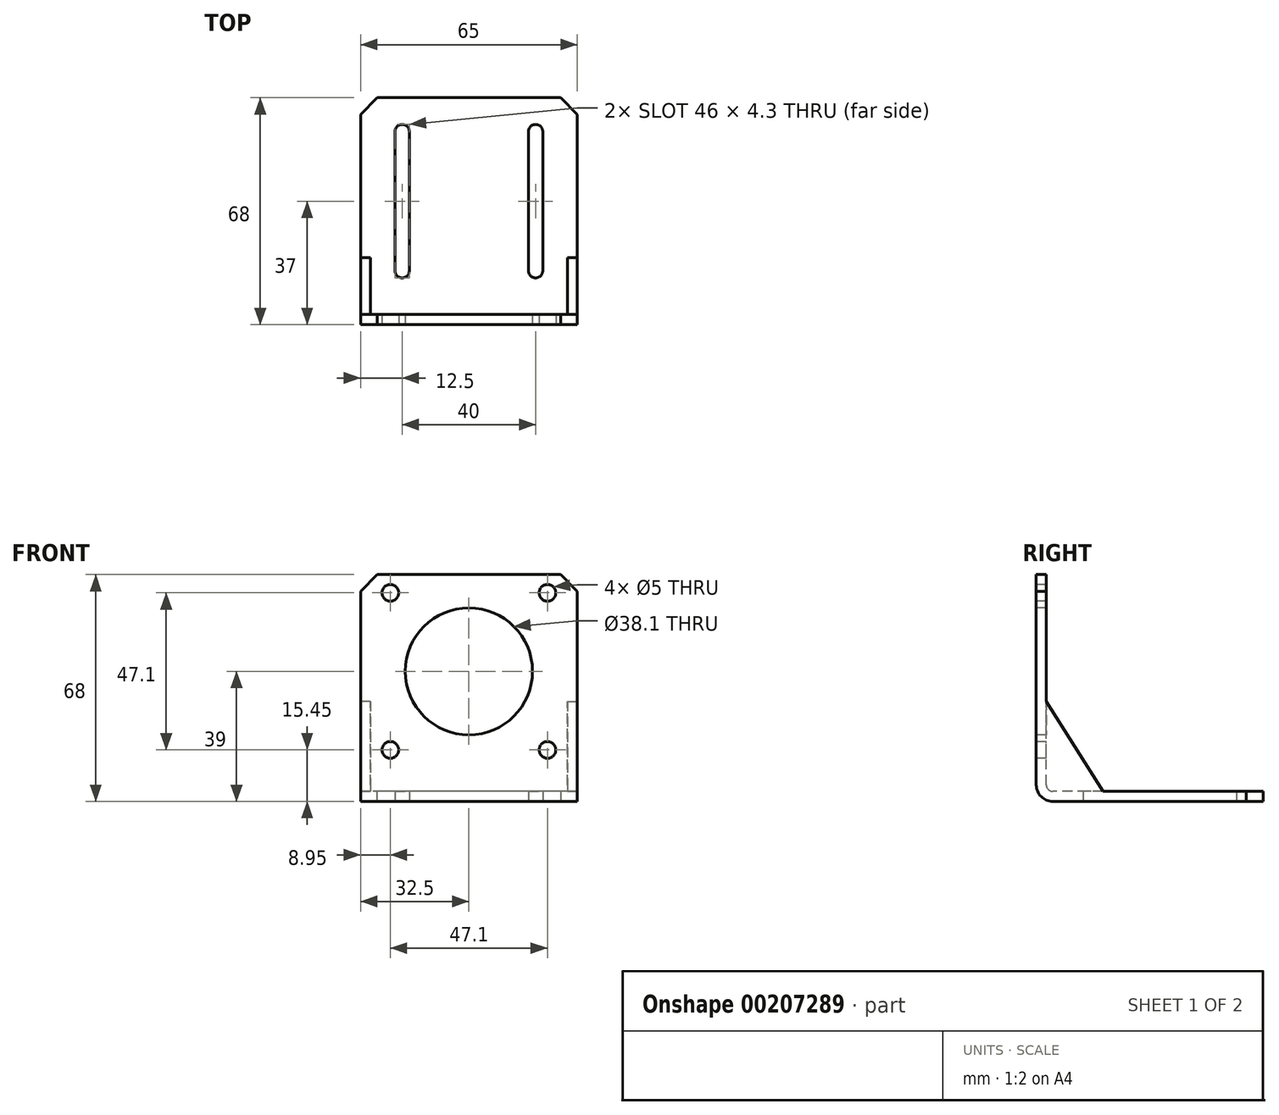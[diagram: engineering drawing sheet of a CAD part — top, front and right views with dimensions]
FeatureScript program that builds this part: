
annotation { "Feature Type Name" : "Feature", "Feature Type Description" : "" }
export const myFeature = defineFeature(function(context is Context, id is Id, definition is map)
    precondition{}
    {
        {
            var Q0;
            Q0=qCreatedBy(makeId("Right.planeOp"),FACE);
            var sketch = newSketch(context, id + "F0", { "sketchPlane" : qUnion([Q0])});
            skLineSegment(sketch, "E0", {"start": v(0, 0) * mm, "end": v(68, 0) * mm});
            skLineSegment(sketch, "E1", {"start": v(68, 0) * mm, "end": v(68, 3) * mm});
            skLineSegment(sketch, "E2", {"start": v(68, 3) * mm, "end": v(3, 3) * mm});
            skLineSegment(sketch, "E3", {"start": v(3, 3) * mm, "end": v(3, 68) * mm});
            skLineSegment(sketch, "E4", {"start": v(3, 68) * mm, "end": v(0, 68) * mm});
            skLineSegment(sketch, "E5", {"start": v(0, 68) * mm, "end": v(0, 0) * mm});
            skSolve(sketch);
        }
        {
            var Q0;
            Q0 = qSketchRegion(id + "F0", true);
            extrude(context, id + "F1", {"entities" : qUnion([Q0]), "endBound" : BoundingType.SYMMETRIC, "depth" : 65 * mm});
        }
        {
            var Q0;
            Q0=makeQuery(id+"F1.opExtrude","SWEPT_EDGE",EDGE,{"disambiguationData":[OSD([sQuery(id+"F0.wireOp",EDGE,"E0"),sQuery(id+"F0.wireOp",EDGE,"E5")])]});
            fillet(context, id + "F2", {"entities" : qUnion([Q0]), "radius" : 5 * mm, "tangentPropagation" : true, "allowEdgeOverflow" : false});
        }
        {
            var Q0;
            Q0=makeQuery(id+"F1.opExtrude","SWEPT_EDGE",EDGE,{"disambiguationData":[OSD([sQuery(id+"F0.wireOp",EDGE,"E2"),sQuery(id+"F0.wireOp",EDGE,"E3")])]});
            fillet(context, id + "F3", {"entities" : qUnion([Q0]), "radius" : 2 * mm, "tangentPropagation" : true, "allowEdgeOverflow" : false});
        }
        {
            var Q0;
            Q0=makeQuery(id+"F1.opExtrude","SWEPT_FACE",FACE,{"disambiguationData":[OSD([sQuery(id+"F0.wireOp",EDGE,"E5")])]});
            var sketch = newSketch(context, id + "F4", { "sketchPlane" : qUnion([Q0])});
            skLineSegment(sketch, "E6", {"start": v(0, 68) * mm, "end": v(0, 39) * mm, "construction": true});
            skPoint(sketch, "E6.endSnap0", {"position": v(0, 68) * mm});
            skLineSegment(sketch, "E7.bottom", {"start": v(23.55, 15.45) * mm, "end": v(-23.55, 15.45) * mm, "construction": true});
            skLineSegment(sketch, "E7.top", {"start": v(23.55, 62.55) * mm, "end": v(-23.55, 62.55) * mm, "construction": true});
            skLineSegment(sketch, "E7.left", {"start": v(23.55, 15.45) * mm, "end": v(23.55, 62.55) * mm, "construction": true});
            skLineSegment(sketch, "E7.right", {"start": v(-23.55, 15.45) * mm, "end": v(-23.55, 62.55) * mm, "construction": true});
            skPoint(sketch, "E7.middle", {"position": v(0, 39) * mm});
            skCircle(sketch, "E8", {"center": v(0, 39) * mm, "radius": 19.05 * mm});
            skCircle(sketch, "E9", {"center": v(-23.55, 15.45) * mm, "radius": 2.5 * mm});
            skCircle(sketch, "E10", {"center": v(23.55, 15.45) * mm, "radius": 2.5 * mm});
            skCircle(sketch, "E11", {"center": v(23.55, 62.55) * mm, "radius": 2.5 * mm});
            skCircle(sketch, "E12", {"center": v(-23.55, 62.55) * mm, "radius": 2.5 * mm});
            skSolve(sketch);
        }
        {
            var Q0;
            Q0 = qSketchRegion(id + "F4", true);
            extrude(context, id + "F5", {"entities" : qUnion([Q0]), "operationType" : NewBodyOperationType.REMOVE, "endBound" : BoundingType.THROUGH_ALL, "oppositeDirection" : true, "depth" : 25 * mm});
        }
        {
            var Q0;
            Q0=makeQuery(id+"F1.opExtrude","SWEPT_FACE",FACE,{"disambiguationData":[OSD([sQuery(id+"F0.wireOp",EDGE,"E0")])]});
            var sketch = newSketch(context, id + "F6", { "sketchPlane" : qUnion([Q0])});
            skLineSegment(sketch, "E13", {"start": v(0, -68) * mm, "end": v(0, -60) * mm, "construction": true});
            skPoint(sketch, "E13.endSnap0", {"position": v(0, -68) * mm});
            skLineSegment(sketch, "E14", {"start": v(-20, -60) * mm, "end": v(20, -60) * mm, "construction": true});
            skLineSegment(sketch, "E15", {"start": v(-20, -60) * mm, "end": v(-20, -57.85) * mm, "construction": true});
            skLineSegment(sketch, "E16", {"start": v(-20, -57.85) * mm, "end": v(-20, -16.15) * mm, "construction": true});
            skLineSegment(sketch, "E17", {"start": v(20, -60) * mm, "end": v(20, -57.85) * mm, "construction": true});
            skLineSegment(sketch, "E18", {"start": v(20, -57.85) * mm, "end": v(20, -16.15) * mm, "construction": true});
            skLineSegment(sketch, "E19", {"start": v(-20, -16.15) * mm, "end": v(-20, -14) * mm, "construction": true});
            skLineSegment(sketch, "E20", {"start": v(20, -16.15) * mm, "end": v(20, -14) * mm, "construction": true});
            skArc(sketch, "E21.0.startCap", {"start": v(-17.85, -57.85) * mm, "mid": v(-20, -60) * mm, "end": v(-22.15, -57.85) * mm});
            skArc(sketch, "E21.0.endCap", {"start": v(-22.15, -16.15) * mm, "mid": v(-20, -14) * mm, "end": v(-17.85, -16.15) * mm});
            skLineSegment(sketch, "E21.0.left", {"start": v(-22.15, -57.85) * mm, "end": v(-22.15, -16.15) * mm});
            skLineSegment(sketch, "E21.0.right", {"start": v(-17.85, -57.85) * mm, "end": v(-17.85, -16.15) * mm});
            skArc(sketch, "E22.0.startCap", {"start": v(22.15, -57.85) * mm, "mid": v(20, -60) * mm, "end": v(17.85, -57.85) * mm});
            skArc(sketch, "E22.0.endCap", {"start": v(17.85, -16.15) * mm, "mid": v(20, -14) * mm, "end": v(22.15, -16.15) * mm});
            skLineSegment(sketch, "E22.0.left", {"start": v(17.85, -57.85) * mm, "end": v(17.85, -16.15) * mm});
            skLineSegment(sketch, "E22.0.right", {"start": v(22.15, -57.85) * mm, "end": v(22.15, -16.15) * mm});
            skSolve(sketch);
        }
        {
            var Q0;
            Q0 = qSketchRegion(id + "F6", true);
            extrude(context, id + "F7", {"entities" : qUnion([Q0]), "operationType" : NewBodyOperationType.REMOVE, "endBound" : BoundingType.THROUGH_ALL, "oppositeDirection" : true, "depth" : 25 * mm});
        }
        {
            var Q0;
            Q0=makeQuery(id+"F1.opExtrude","CAP_FACE",FACE,{"disambiguationData":[OSD([sQuery(id+"F0.wireOp",EDGE,"E0"),sQuery(id+"F0.wireOp",EDGE,"E1"),sQuery(id+"F0.wireOp",EDGE,"E2"),sQuery(id+"F0.wireOp",EDGE,"E3"),sQuery(id+"F0.wireOp",EDGE,"E4"),sQuery(id+"F0.wireOp",EDGE,"E5")])],"isStart":false});
            var sketch = newSketch(context, id + "F8", { "sketchPlane" : qUnion([Q0])});
            skLineSegment(sketch, "E23.0", {"start": v(3, 5) * mm, "end": v(3, 30) * mm});
            skArc(sketch, "E24.0", {"start": v(5, 3) * mm, "mid": v(3.59, 3.59) * mm, "end": v(3, 5) * mm});
            skLineSegment(sketch, "E25.0", {"start": v(20, 3) * mm, "end": v(5, 3) * mm});
            skLineSegment(sketch, "E26", {"start": v(3, 30) * mm, "end": v(20, 3) * mm});
            skPoint(sketch, "E27.orphan", {"position": v(3, 68) * mm});
            skPoint(sketch, "E28.orphan", {"position": v(68, 3) * mm});
            skSolve(sketch);
        }
        {
            var Q0;
            Q0 = qSketchRegion(id + "F8", true);
            extrude(context, id + "F9", {"entities" : qUnion([Q0]), "operationType" : NewBodyOperationType.ADD, "oppositeDirection" : true, "depth" : 3 * mm});
        }
        {
            var Q0;
            Q0=makeQuery(id+"F1.opExtrude","CAP_FACE",FACE,{"disambiguationData":[OSD([sQuery(id+"F0.wireOp",EDGE,"E0"),sQuery(id+"F0.wireOp",EDGE,"E1"),sQuery(id+"F0.wireOp",EDGE,"E2"),sQuery(id+"F0.wireOp",EDGE,"E3"),sQuery(id+"F0.wireOp",EDGE,"E4"),sQuery(id+"F0.wireOp",EDGE,"E5")])],"isStart":true});
            var sketch = newSketch(context, id + "F10", { "sketchPlane" : qUnion([Q0])});
            skLineSegment(sketch, "E29.0.0", {"start": v(-3, 30) * mm, "end": v(-20, 3) * mm});
            skLineSegment(sketch, "E29.0.1", {"start": v(-20, 3) * mm, "end": v(-5, 3) * mm});
            skArc(sketch, "E29.0.2", {"start": v(-5, 3) * mm, "mid": v(-3.59, 3.59) * mm, "end": v(-3, 5) * mm});
            skLineSegment(sketch, "E29.0.3", {"start": v(-3, 5) * mm, "end": v(-3, 30) * mm});
            skSolve(sketch);
        }
        {
            var Q0;
            Q0 = qSketchRegion(id + "F10", true);
            extrude(context, id + "F11", {"entities" : qUnion([Q0]), "operationType" : NewBodyOperationType.ADD, "oppositeDirection" : true, "depth" : 3 * mm});
        }
        {
            var Q0;
            Q0=makeQuery(id+"F1.opExtrude","CAP_EDGE",EDGE,{"disambiguationData":[OSD([sQuery(id+"F0.wireOp",EDGE,"E4")])],"isStart":false});
            var Q1;
            Q1=makeQuery(id+"F1.opExtrude","CAP_EDGE",EDGE,{"disambiguationData":[OSD([sQuery(id+"F0.wireOp",EDGE,"E1")])],"isStart":false});
            var Q2;
            Q2=makeQuery(id+"F1.opExtrude","CAP_EDGE",EDGE,{"disambiguationData":[OSD([sQuery(id+"F0.wireOp",EDGE,"E1")])],"isStart":true});
            var Q3;
            Q3=makeQuery(id+"F1.opExtrude","CAP_EDGE",EDGE,{"disambiguationData":[OSD([sQuery(id+"F0.wireOp",EDGE,"E4")])],"isStart":true});
            chamfer(context, id + "F12", {"entities" : qUnion([Q0, Q1, Q2, Q3]), "width" : 5 * mm, "tangentPropagation" : true});
        }
    });
